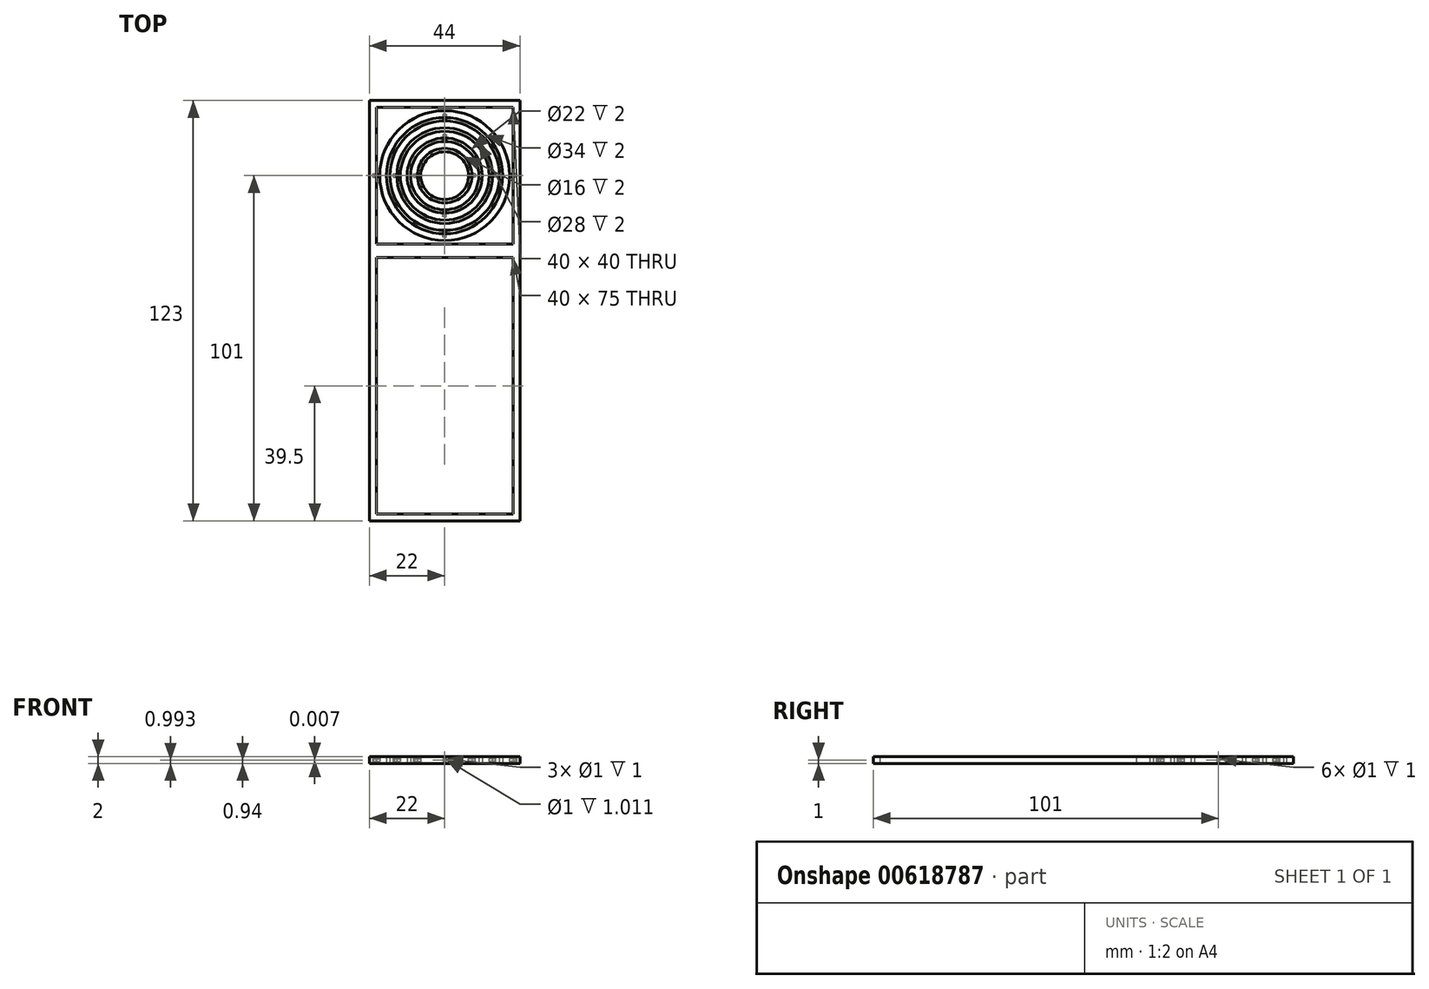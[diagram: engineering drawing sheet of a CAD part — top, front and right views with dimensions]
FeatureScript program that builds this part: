
annotation { "Feature Type Name" : "Feature", "Feature Type Description" : "" }
export const myFeature = defineFeature(function(context is Context, id is Id, definition is map)
    precondition{}
    {
        {
            var Q0;
            Q0=qCreatedBy(makeId("Top.planeOp"),FACE);
            var sketch = newSketch(context, id + "F0", { "sketchPlane" : qUnion([Q0])});
            skLineSegment(sketch, "E0.bottom", {"start": v(0, 0) * mm, "end": v(40, 0) * mm});
            skLineSegment(sketch, "E0.top", {"start": v(0, -75) * mm, "end": v(40, -75) * mm});
            skLineSegment(sketch, "E0.left", {"start": v(0, 0) * mm, "end": v(0, -75) * mm});
            skLineSegment(sketch, "E0.right", {"start": v(40, 0) * mm, "end": v(40, -75) * mm});
            skLineSegment(sketch, "E1.0", {"start": v(-2, -77) * mm, "end": v(42, -77) * mm});
            skLineSegment(sketch, "E1.1", {"start": v(-2, 2) * mm, "end": v(-2, -77) * mm});
            skLineSegment(sketch, "E1.2", {"start": v(-2, 2) * mm, "end": v(42, 2) * mm});
            skLineSegment(sketch, "E1.3", {"start": v(42, 2) * mm, "end": v(42, -77) * mm});
            skLineSegment(sketch, "E2.bottom", {"start": v(12.5, 0) * mm, "end": v(27.5, 0) * mm});
            skLineSegment(sketch, "E2.top", {"start": v(12.5, -30) * mm, "end": v(27.5, -30) * mm});
            skLineSegment(sketch, "E2.left", {"start": v(12.5, 0) * mm, "end": v(12.5, -30) * mm});
            skLineSegment(sketch, "E2.right", {"start": v(27.5, 0) * mm, "end": v(27.5, -30) * mm});
            skLineSegment(sketch, "E3.top", {"start": v(-2, 46) * mm, "end": v(42, 46) * mm});
            skLineSegment(sketch, "E3.left", {"start": v(-2, 2) * mm, "end": v(-2, 46) * mm});
            skLineSegment(sketch, "E3.right", {"start": v(42, 2) * mm, "end": v(42, 46) * mm});
            skLineSegment(sketch, "E4.0", {"start": v(40, 4) * mm, "end": v(40, 44) * mm});
            skLineSegment(sketch, "E4.1", {"start": v(0, 4) * mm, "end": v(40, 4) * mm});
            skLineSegment(sketch, "E4.2", {"start": v(0, 4) * mm, "end": v(0, 44) * mm});
            skLineSegment(sketch, "E4.3", {"start": v(0, 44) * mm, "end": v(40, 44) * mm});
            skLineSegment(sketch, "E5", {"start": v(20, 44) * mm, "end": v(20, 4) * mm, "construction": true});
            skLineSegment(sketch, "E6", {"start": v(0, 24) * mm, "end": v(40, 24) * mm, "construction": true});
            skCircle(sketch, "E7", {"center": v(20, 24) * mm, "radius": 19 * mm});
            skCircle(sketch, "E8.0", {"center": v(20, 24) * mm, "radius": 17 * mm});
            skCircle(sketch, "E9", {"center": v(20, 24) * mm, "radius": 16 * mm});
            skCircle(sketch, "E10.0", {"center": v(20, 24) * mm, "radius": 14 * mm});
            skCircle(sketch, "E11", {"center": v(20, 24) * mm, "radius": 13 * mm});
            skCircle(sketch, "E12.0", {"center": v(20, 24) * mm, "radius": 11 * mm});
            skCircle(sketch, "E13", {"center": v(20, 24) * mm, "radius": 10 * mm});
            skCircle(sketch, "E14.0", {"center": v(20, 24) * mm, "radius": 8 * mm});
            skCircle(sketch, "E15", {"center": v(20, 24) * mm, "radius": 7 * mm});
            skSolve(sketch);
        }
        {
            var Q0;
            Q0=makeQuery(id+"F0.imprint","IMPRINT",FACE,{"disambiguationData":[TD([[makeQuery(id+"F0.imprint","IMPRINT",EDGE,{"derivedFrom":sQuery(id+"F0.wireOp",EDGE,"E0.top")}),-1.0]])]});
            var Q1;
            Q1=makeQuery(id+"F0.imprint","IMPRINT",FACE,{"disambiguationData":[TD([[makeQuery(id+"F0.imprint","IMPRINT",EDGE,{"derivedFrom":sQuery(id+"F0.wireOp",EDGE,"E2.bottom")}),-1.0]])]});
            var Q2;
            Q2=makeQuery(id+"F0.imprint","IMPRINT",FACE,{"disambiguationData":[TD([[makeQuery(id+"F0.imprint","IMPRINT",EDGE,{"derivedFrom":sQuery(id+"F0.wireOp",EDGE,"E1.2")}),1.0]])]});
            var Q3;
            Q3=makeQuery(id+"F0.imprint","IMPRINT",FACE,{"disambiguationData":[TD([[makeQuery(id+"F0.imprint","IMPRINT",EDGE,{"derivedFrom":sQuery(id+"F0.wireOp",EDGE,"E7")}),1.0]])]});
            var Q4;
            Q4=makeQuery(id+"F0.imprint","IMPRINT",FACE,{"disambiguationData":[TD([[makeQuery(id+"F0.imprint","IMPRINT",EDGE,{"derivedFrom":sQuery(id+"F0.wireOp",EDGE,"E9")}),1.0]])]});
            var Q5;
            Q5=makeQuery(id+"F0.imprint","IMPRINT",FACE,{"disambiguationData":[TD([[makeQuery(id+"F0.imprint","IMPRINT",EDGE,{"derivedFrom":sQuery(id+"F0.wireOp",EDGE,"E11")}),1.0]])]});
            var Q6;
            Q6=makeQuery(id+"F0.imprint","IMPRINT",FACE,{"disambiguationData":[TD([[makeQuery(id+"F0.imprint","IMPRINT",EDGE,{"derivedFrom":sQuery(id+"F0.wireOp",EDGE,"E13")}),1.0]])]});
            var Q7;
            Q7=makeQuery(id+"F0.imprint","IMPRINT",FACE,{"disambiguationData":[TD([[makeQuery(id+"F0.imprint","IMPRINT",EDGE,{"derivedFrom":sQuery(id+"F0.wireOp",EDGE,"E15")}),1.0]])]});
            extrude(context, id + "F1", {"entities" : qUnion([Q0, Q1, Q2, Q3, Q4, Q5, Q6, Q7]), "depth" : 2 * mm, "offsetDistance" : 25 * mm});
        }
        {
            var Q0;
            Q0=qCreatedBy(makeId("Front.planeOp"),FACE);
            cPlane(context, id + "F2", {"entities" : qUnion([Q0]), "cplaneType" : CPlaneType.OFFSET, "offset" : 13 * mm, "oppositeDirection" : true, "width" : 150 * mm, "height" : 150 * mm});
        }
        {
            var Q0;
            Q0=qCreatedBy(id+"F2.planeOp",FACE);
            var sketch = newSketch(context, id + "F3", { "sketchPlane" : qUnion([Q0])});
            skLineSegment(sketch, "E16.0", {"start": v(9, 2) * mm, "end": v(31, 2) * mm});
            skLineSegment(sketch, "E17.0", {"start": v(9, 0) * mm, "end": v(31, 0) * mm});
            skLineSegment(sketch, "E18", {"start": v(20, 2) * mm, "end": v(20, 0) * mm, "construction": true});
            skLineSegment(sketch, "E19", {"start": v(19.5, 1) * mm, "end": v(20.6, 1) * mm, "construction": true});
            skCircle(sketch, "E20", {"center": v(20, 1) * mm, "radius": 0.5 * mm});
            skSolve(sketch);
        }
        {
            var Q0;
            Q0 = qSketchRegion(id + "F3", true);
            extrude(context, id + "F4", {"entities" : qUnion([Q0]), "operationType" : NewBodyOperationType.REMOVE, "depth" : 1 * mm, "offsetDistance" : 25 * mm, "hasSecondDirection" : true, "secondDirectionOppositeDirection" : true, "secondDirectionDepth" : .2 * mm});
        }
        {
            var Q0;
            Q0=qCreatedBy(makeId("Front.planeOp"),FACE);
            cPlane(context, id + "F5", {"entities" : qUnion([Q0]), "cplaneType" : CPlaneType.OFFSET, "offset" : 35 * mm, "oppositeDirection" : true, "width" : 150 * mm, "height" : 150 * mm});
        }
        {
            var Q0;
            Q0=qCreatedBy(id+"F5.planeOp",FACE);
            var sketch = newSketch(context, id + "F6", { "sketchPlane" : qUnion([Q0])});
            skLineSegment(sketch, "E21.0", {"start": v(9, 2) * mm, "end": v(31, 2) * mm});
            skLineSegment(sketch, "E22.0", {"start": v(9, 0) * mm, "end": v(31, 0) * mm});
            skLineSegment(sketch, "E23", {"start": v(20, 2) * mm, "end": v(20, 0) * mm, "construction": true});
            skLineSegment(sketch, "E24", {"start": v(20, 0) * mm, "end": v(20, -0.04) * mm, "construction": true});
            skLineSegment(sketch, "E25", {"start": v(20, 0.94) * mm, "end": v(19.44, 0.94) * mm, "construction": true});
            skLineSegment(sketch, "E26", {"start": v(19.44, 0.94) * mm, "end": v(20.62, 0.94) * mm, "construction": true});
            skCircle(sketch, "E27", {"center": v(20, 0.94) * mm, "radius": 0.5 * mm});
            skSolve(sketch);
        }
        {
            var Q0;
            Q0 = qSketchRegion(id + "F6", true);
            extrude(context, id + "F7", {"entities" : qUnion([Q0]), "operationType" : NewBodyOperationType.REMOVE, "oppositeDirection" : true, "depth" : 1 * mm, "offsetDistance" : 25 * mm, "hasSecondDirection" : true, "secondDirectionOppositeDirection" : false, "secondDirectionDepth" : .2 * mm});
        }
        {
            var Q0;
            Q0=qCreatedBy(makeId("Front.planeOp"),FACE);
            cPlane(context, id + "F8", {"entities" : qUnion([Q0]), "cplaneType" : CPlaneType.OFFSET, "offset" : 7 * mm, "oppositeDirection" : true, "width" : 150 * mm, "height" : 150 * mm});
        }
        {
            var Q0;
            Q0=qCreatedBy(id+"F8.planeOp",FACE);
            var sketch = newSketch(context, id + "F9", { "sketchPlane" : qUnion([Q0])});
            skLineSegment(sketch, "E28.0", {"start": v(3, 2) * mm, "end": v(37, 2) * mm});
            skLineSegment(sketch, "E29.0", {"start": v(3, 0) * mm, "end": v(37, 0) * mm});
            skLineSegment(sketch, "E30", {"start": v(20, 0) * mm, "end": v(20, 2) * mm, "construction": true});
            skLineSegment(sketch, "E31", {"start": v(20, 1) * mm, "end": v(19.29, 1) * mm, "construction": true});
            skCircle(sketch, "E32", {"center": v(20, 1) * mm, "radius": 0.5 * mm});
            skSolve(sketch);
        }
        {
            var Q0;
            Q0 = qSketchRegion(id + "F9", true);
            extrude(context, id + "F10", {"entities" : qUnion([Q0]), "operationType" : NewBodyOperationType.REMOVE, "depth" : 1 * mm, "offsetDistance" : 25 * mm, "hasSecondDirection" : true, "secondDirectionOppositeDirection" : true, "secondDirectionDepth" : .2 * mm});
        }
        {
            var Q0;
            Q0=qCreatedBy(makeId("Front.planeOp"),FACE);
            cPlane(context, id + "F11", {"entities" : qUnion([Q0]), "cplaneType" : CPlaneType.OFFSET, "offset" : 41 * mm, "oppositeDirection" : true, "width" : 150 * mm, "height" : 150 * mm});
        }
        {
            var Q0;
            Q0=qCreatedBy(id+"F11.planeOp",FACE);
            var sketch = newSketch(context, id + "F12", { "sketchPlane" : qUnion([Q0])});
            skLineSegment(sketch, "E33.0", {"start": v(3, 2) * mm, "end": v(37, 2) * mm});
            skLineSegment(sketch, "E34.0", {"start": v(3, 0) * mm, "end": v(37, 0) * mm});
            skLineSegment(sketch, "E35", {"start": v(20, 0) * mm, "end": v(20, 2) * mm, "construction": true});
            skLineSegment(sketch, "E36", {"start": v(19.44, 1) * mm, "end": v(20, 1) * mm, "construction": true});
            skCircle(sketch, "E37", {"center": v(20, 1) * mm, "radius": 0.5 * mm});
            skSolve(sketch);
        }
        {
            var Q0;
            Q0 = qSketchRegion(id + "F12", true);
            extrude(context, id + "F13", {"entities" : qUnion([Q0]), "operationType" : NewBodyOperationType.REMOVE, "oppositeDirection" : true, "depth" : 1 * mm, "offsetDistance" : 25 * mm, "hasSecondDirection" : true, "secondDirectionOppositeDirection" : false, "secondDirectionDepth" : .2 * mm});
        }
        {
            var Q0;
            Q0=qCreatedBy(makeId("Right.planeOp"),FACE);
            cPlane(context, id + "F14", {"entities" : qUnion([Q0]), "cplaneType" : CPlaneType.OFFSET, "offset" : 6 * mm, "width" : 150 * mm, "height" : 150 * mm});
        }
        {
            var Q0;
            Q0=qCreatedBy(id+"F14.planeOp",FACE);
            var sketch = newSketch(context, id + "F15", { "sketchPlane" : qUnion([Q0])});
            skLineSegment(sketch, "E38.0", {"start": v(10, 2) * mm, "end": v(38, 2) * mm});
            skLineSegment(sketch, "E39.0", {"start": v(10, 0) * mm, "end": v(38, 0) * mm});
            skLineSegment(sketch, "E40", {"start": v(24.24, 1) * mm, "end": v(23.72, 1) * mm, "construction": true});
            skCircle(sketch, "E41", {"center": v(24, 1) * mm, "radius": 0.5 * mm});
            skSolve(sketch);
        }
        {
            var Q0;
            Q0=makeQuery(id+"F15.imprint","IMPRINT",FACE,{"disambiguationData":[TD([[makeQuery(id+"F15.imprint","IMPRINT",EDGE,{"derivedFrom":sQuery(id+"F15.wireOp",EDGE,"E41")}),1.0]])]});
            extrude(context, id + "F16", {"entities" : qUnion([Q0]), "operationType" : NewBodyOperationType.REMOVE, "oppositeDirection" : true, "depth" : 1 * mm, "offsetDistance" : 25 * mm, "hasSecondDirection" : true, "secondDirectionOppositeDirection" : false, "secondDirectionDepth" : .2 * mm});
        }
        {
            var Q0;
            Q0=qCreatedBy(makeId("Right.planeOp"),FACE);
            cPlane(context, id + "F17", {"entities" : qUnion([Q0]), "cplaneType" : CPlaneType.OFFSET, "offset" : 34 * mm, "width" : 150 * mm, "height" : 150 * mm});
        }
        {
            var Q0;
            Q0=qCreatedBy(id+"F17.planeOp",FACE);
            var sketch = newSketch(context, id + "F18", { "sketchPlane" : qUnion([Q0])});
            skLineSegment(sketch, "E42.0", {"start": v(10, 0) * mm, "end": v(38, 0) * mm});
            skLineSegment(sketch, "E43.0", {"start": v(10, 2) * mm, "end": v(38, 2) * mm});
            skLineSegment(sketch, "E44", {"start": v(24, 0) * mm, "end": v(24, 2) * mm, "construction": true});
            skLineSegment(sketch, "E45", {"start": v(24.2, 1) * mm, "end": v(23.66, 1) * mm, "construction": true});
            skCircle(sketch, "E46", {"center": v(24, 1) * mm, "radius": 0.5 * mm});
            skSolve(sketch);
        }
        {
            var Q0;
            Q0 = qSketchRegion(id + "F18", true);
            extrude(context, id + "F19", {"entities" : qUnion([Q0]), "operationType" : NewBodyOperationType.REMOVE, "depth" : 1 * mm, "offsetDistance" : 25 * mm, "hasSecondDirection" : true, "secondDirectionOppositeDirection" : true, "secondDirectionDepth" : .2 * mm});
        }
        {
            var Q0;
            Q0=makeQuery(id+"F1.opExtrude","SWEPT_FACE",FACE,{"disambiguationData":[OSD([sQuery(id+"F0.wireOp",EDGE,"E4.2")])]});
            var sketch = newSketch(context, id + "F20", { "sketchPlane" : qUnion([Q0])});
            skPoint(sketch, "E47.0", {"position": v(24, 0) * mm});
            skLineSegment(sketch, "E48", {"start": v(24, 0) * mm, "end": v(24, 2) * mm, "construction": true});
            skLineSegment(sketch, "E49", {"start": v(24.56, 1) * mm, "end": v(23.4, 1) * mm, "construction": true});
            skCircle(sketch, "E50", {"center": v(24, 1) * mm, "radius": 0.5 * mm});
            skSolve(sketch);
        }
        {
            var Q0;
            Q0=makeQuery(id+"F20.imprint","IMPRINT",FACE,{"disambiguationData":[TD([[makeQuery(id+"F20.imprint","IMPRINT",EDGE,{"derivedFrom":sQuery(id+"F20.wireOp",EDGE,"E50")}),1.0]])]});
            extrude(context, id + "F21", {"entities" : qUnion([Q0]), "operationType" : NewBodyOperationType.REMOVE, "oppositeDirection" : true, "depth" : 1 * mm, "offsetDistance" : 25 * mm});
        }
        {
            var Q0;
            Q0=makeQuery(id+"F1.opExtrude","SWEPT_FACE",FACE,{"disambiguationData":[OSD([sQuery(id+"F0.wireOp",EDGE,"E4.0")])]});
            var sketch = newSketch(context, id + "F22", { "sketchPlane" : qUnion([Q0])});
            skLineSegment(sketch, "E51", {"start": v(-24, 0) * mm, "end": v(-24, 2) * mm, "construction": true});
            skLineSegment(sketch, "E52", {"start": v(-24.46, 1) * mm, "end": v(-23.58, 1) * mm, "construction": true});
            skCircle(sketch, "E53", {"center": v(-24, 1) * mm, "radius": 0.5 * mm});
            skSolve(sketch);
        }
        {
            var Q0;
            Q0=makeQuery(id+"F22.imprint","IMPRINT",FACE,{"disambiguationData":[TD([[makeQuery(id+"F22.imprint","IMPRINT",EDGE,{"derivedFrom":sQuery(id+"F22.wireOp",EDGE,"E53")}),1.0]])]});
            extrude(context, id + "F23", {"entities" : qUnion([Q0]), "operationType" : NewBodyOperationType.REMOVE, "oppositeDirection" : true, "depth" : 1 * mm, "offsetDistance" : 25 * mm});
        }
        {
            var Q0;
            Q0=qCreatedBy(makeId("Right.planeOp"),FACE);
            cPlane(context, id + "F24", {"entities" : qUnion([Q0]), "cplaneType" : CPlaneType.OFFSET, "offset" : 1 * mm, "width" : 150 * mm, "height" : 150 * mm});
        }
        {
            var Q0;
            Q0=qCreatedBy(id+"F24.planeOp",FACE);
            var sketch = newSketch(context, id + "F25", { "sketchPlane" : qUnion([Q0])});
            skPoint(sketch, "E54.0", {"position": v(24, 0) * mm});
            skLineSegment(sketch, "E55", {"start": v(24, 0) * mm, "end": v(24, 2) * mm, "construction": true});
            skLineSegment(sketch, "E56", {"start": v(24.48, 1) * mm, "end": v(23.55, 1) * mm, "construction": true});
            skCircle(sketch, "E57", {"center": v(24, 1) * mm, "radius": 0.35 * mm});
            skSolve(sketch);
        }
        {
            var Q0;
            Q0=qCreatedBy(makeId("Right.planeOp"),FACE);
            cPlane(context, id + "F26", {"entities" : qUnion([Q0]), "cplaneType" : CPlaneType.OFFSET, "offset" : 12 * mm, "width" : 150 * mm, "height" : 150 * mm});
        }
        {
            var Q0;
            Q0=qCreatedBy(id+"F26.planeOp",FACE);
            var sketch = newSketch(context, id + "F27", { "sketchPlane" : qUnion([Q0])});
            skLineSegment(sketch, "E58.0", {"start": v(16, 2) * mm, "end": v(32, 2) * mm});
            skLineSegment(sketch, "E59.0", {"start": v(16, 0) * mm, "end": v(32, 0) * mm});
            skLineSegment(sketch, "E60", {"start": v(24, 2) * mm, "end": v(24, 0) * mm, "construction": true});
            skLineSegment(sketch, "E61", {"start": v(24, 0) * mm, "end": v(23.98, -0.05) * mm, "construction": true});
            skCircle(sketch, "E62", {"center": v(24, 1) * mm, "radius": 0.5 * mm});
            skSolve(sketch);
        }
        {
            var Q0;
            Q0 = qSketchRegion(id + "F27", true);
            extrude(context, id + "F28", {"entities" : qUnion([Q0]), "operationType" : NewBodyOperationType.REMOVE, "oppositeDirection" : true, "depth" : 1 * mm, "offsetDistance" : 25 * mm, "hasSecondDirection" : true, "secondDirectionOppositeDirection" : false, "secondDirectionDepth" : .2 * mm});
        }
        {
            var Q0;
            Q0=qCreatedBy(makeId("Right.planeOp"),FACE);
            cPlane(context, id + "F29", {"entities" : qUnion([Q0]), "cplaneType" : CPlaneType.OFFSET, "offset" : 28 * mm, "width" : 150 * mm, "height" : 150 * mm});
        }
        {
            var Q0;
            Q0=qCreatedBy(id+"F29.planeOp",FACE);
            var sketch = newSketch(context, id + "F30", { "sketchPlane" : qUnion([Q0])});
            skLineSegment(sketch, "E63.0", {"start": v(16, 2) * mm, "end": v(32, 2) * mm});
            skLineSegment(sketch, "E64.0", {"start": v(16, 0) * mm, "end": v(32, 0) * mm});
            skLineSegment(sketch, "E65", {"start": v(24, 2) * mm, "end": v(24, 0) * mm, "construction": true});
            skLineSegment(sketch, "E66", {"start": v(24, 0) * mm, "end": v(24.02, -0.07) * mm, "construction": true});
            skCircle(sketch, "E67", {"center": v(24, 1) * mm, "radius": 0.5 * mm});
            skSolve(sketch);
        }
        {
            var Q0;
            Q0 = qSketchRegion(id + "F30", true);
            extrude(context, id + "F31", {"entities" : qUnion([Q0]), "operationType" : NewBodyOperationType.REMOVE, "depth" : 1 * mm, "offsetDistance" : 25 * mm, "hasSecondDirection" : true, "secondDirectionOppositeDirection" : true, "secondDirectionDepth" : .2 * mm});
        }
        {
            var Q0;
            Q0=makeQuery(id+"F25.imprint","IMPRINT",FACE,{"disambiguationData":[TD([[makeQuery(id+"F25.imprint","IMPRINT",EDGE,{"derivedFrom":sQuery(id+"F25.wireOp",EDGE,"E57")}),1.0]])]});
            extrude(context, id + "F32", {"entities" : qUnion([Q0]), "operationType" : NewBodyOperationType.ADD, "oppositeDirection" : true, "depth" : 1.7 * mm, "offsetDistance" : 25 * mm, "hasSecondDirection" : true, "secondDirectionOppositeDirection" : false, "secondDirectionDepth" : .2 * mm});
        }
        {
            var Q0;
            Q0=qCreatedBy(makeId("Right.planeOp"),FACE);
            cPlane(context, id + "F33", {"entities" : qUnion([Q0]), "cplaneType" : CPlaneType.OFFSET, "offset" : 39 * mm, "width" : 150 * mm, "height" : 150 * mm});
        }
        {
            var Q0;
            Q0=qCreatedBy(id+"F33.planeOp",FACE);
            var sketch = newSketch(context, id + "F34", { "sketchPlane" : qUnion([Q0])});
            skLineSegment(sketch, "E68.0", {"start": v(5, 0) * mm, "end": v(43, 0) * mm});
            skLineSegment(sketch, "E69.0", {"start": v(5, 2) * mm, "end": v(43, 2) * mm});
            skPoint(sketch, "E70.0", {"position": v(24, 0) * mm});
            skLineSegment(sketch, "E71", {"start": v(24, 0) * mm, "end": v(24, 2) * mm, "construction": true});
            skLineSegment(sketch, "E72", {"start": v(24.56, 1) * mm, "end": v(23.48, 1) * mm, "construction": true});
            skCircle(sketch, "E73", {"center": v(24, 1) * mm, "radius": 0.35 * mm});
            skSolve(sketch);
        }
        {
            var Q0;
            Q0=makeQuery(id+"F34.imprint","IMPRINT",FACE,{"disambiguationData":[TD([[makeQuery(id+"F34.imprint","IMPRINT",EDGE,{"derivedFrom":sQuery(id+"F34.wireOp",EDGE,"E73")}),1.0]])]});
            extrude(context, id + "F35", {"entities" : qUnion([Q0]), "operationType" : NewBodyOperationType.ADD, "depth" : 1.7 * mm, "offsetDistance" : 25 * mm, "hasSecondDirection" : true, "secondDirectionOppositeDirection" : true, "secondDirectionDepth" : .2 * mm});
        }
        {
            var Q0;
            Q0=qCreatedBy(makeId("Right.planeOp"),FACE);
            cPlane(context, id + "F36", {"entities" : qUnion([Q0]), "cplaneType" : CPlaneType.OFFSET, "offset" : 7 * mm, "width" : 150 * mm, "height" : 150 * mm});
        }
        {
            var Q0;
            Q0=qCreatedBy(id+"F36.planeOp",FACE);
            var sketch = newSketch(context, id + "F37", { "sketchPlane" : qUnion([Q0])});
            skLineSegment(sketch, "E74.0", {"start": v(5, 0) * mm, "end": v(43, 0) * mm});
            skPoint(sketch, "E75.0", {"position": v(24, 0) * mm});
            skLineSegment(sketch, "E76.0", {"start": v(11, 2) * mm, "end": v(37, 2) * mm});
            skLineSegment(sketch, "E77", {"start": v(24, 0) * mm, "end": v(24, 2) * mm, "construction": true});
            skLineSegment(sketch, "E78", {"start": v(24.67, 1) * mm, "end": v(23.38, 1) * mm, "construction": true});
            skCircle(sketch, "E79", {"center": v(24, 1) * mm, "radius": 0.35 * mm});
            skSolve(sketch);
        }
        {
            var Q0;
            Q0=makeQuery(id+"F37.imprint","IMPRINT",FACE,{"disambiguationData":[TD([[makeQuery(id+"F37.imprint","IMPRINT",EDGE,{"derivedFrom":sQuery(id+"F37.wireOp",EDGE,"E79")}),1.0]])]});
            extrude(context, id + "F38", {"entities" : qUnion([Q0]), "operationType" : NewBodyOperationType.ADD, "oppositeDirection" : true, "depth" : 1.7 * mm, "offsetDistance" : 25 * mm, "hasSecondDirection" : true, "secondDirectionOppositeDirection" : false, "secondDirectionDepth" : .2 * mm});
        }
        {
            var Q0;
            Q0=qCreatedBy(makeId("Right.planeOp"),FACE);
            cPlane(context, id + "F39", {"entities" : qUnion([Q0]), "cplaneType" : CPlaneType.OFFSET, "offset" : 33 * mm, "width" : 150 * mm, "height" : 150 * mm});
        }
        {
            var Q0;
            Q0=qCreatedBy(id+"F39.planeOp",FACE);
            var sketch = newSketch(context, id + "F40", { "sketchPlane" : qUnion([Q0])});
            skLineSegment(sketch, "E80.0", {"start": v(11, 2) * mm, "end": v(37, 2) * mm});
            skLineSegment(sketch, "E81.0", {"start": v(5, 0) * mm, "end": v(43, 0) * mm});
            skPoint(sketch, "E82.0", {"position": v(24, 0) * mm});
            skLineSegment(sketch, "E83", {"start": v(24, 0) * mm, "end": v(24, 2) * mm, "construction": true});
            skLineSegment(sketch, "E84", {"start": v(22.86, 1) * mm, "end": v(25.17, 1) * mm, "construction": true});
            skCircle(sketch, "E85", {"center": v(24, 1) * mm, "radius": 0.35 * mm});
            skSolve(sketch);
        }
        {
            var Q0;
            Q0=makeQuery(id+"F40.imprint","IMPRINT",FACE,{"disambiguationData":[TD([[makeQuery(id+"F40.imprint","IMPRINT",EDGE,{"derivedFrom":sQuery(id+"F40.wireOp",EDGE,"E85")}),1.0]])]});
            extrude(context, id + "F41", {"entities" : qUnion([Q0]), "operationType" : NewBodyOperationType.ADD, "depth" : 1.7 * mm, "offsetDistance" : 25 * mm, "hasSecondDirection" : true, "secondDirectionOppositeDirection" : true, "secondDirectionDepth" : .2 * mm});
        }
        {
            var Q0;
            Q0=qCreatedBy(makeId("Right.planeOp"),FACE);
            cPlane(context, id + "F42", {"entities" : qUnion([Q0]), "cplaneType" : CPlaneType.OFFSET, "offset" : 13 * mm, "width" : 150 * mm, "height" : 150 * mm});
        }
        {
            var Q0;
            Q0=qCreatedBy(id+"F42.planeOp",FACE);
            var sketch = newSketch(context, id + "F43", { "sketchPlane" : qUnion([Q0])});
            skLineSegment(sketch, "E86.0", {"start": v(17, 2) * mm, "end": v(31, 2) * mm});
            skLineSegment(sketch, "E87.0", {"start": v(5, 0) * mm, "end": v(43, 0) * mm});
            skPoint(sketch, "E88.0", {"position": v(24, 0) * mm});
            skLineSegment(sketch, "E89", {"start": v(24, 0) * mm, "end": v(24, 2) * mm, "construction": true});
            skLineSegment(sketch, "E90", {"start": v(24.58, 1) * mm, "end": v(23.34, 1) * mm, "construction": true});
            skCircle(sketch, "E91", {"center": v(24, 1) * mm, "radius": 0.35 * mm});
            skSolve(sketch);
        }
        {
            var Q0;
            Q0=makeQuery(id+"F43.imprint","IMPRINT",FACE,{"disambiguationData":[TD([[makeQuery(id+"F43.imprint","IMPRINT",EDGE,{"derivedFrom":sQuery(id+"F43.wireOp",EDGE,"E91")}),1.0]])]});
            extrude(context, id + "F44", {"entities" : qUnion([Q0]), "operationType" : NewBodyOperationType.ADD, "oppositeDirection" : true, "depth" : 1.7 * mm, "offsetDistance" : 25 * mm, "hasSecondDirection" : true, "secondDirectionOppositeDirection" : false, "secondDirectionDepth" : .2 * mm});
        }
        {
            var Q0;
            Q0=qCreatedBy(makeId("Right.planeOp"),FACE);
            cPlane(context, id + "F45", {"entities" : qUnion([Q0]), "cplaneType" : CPlaneType.OFFSET, "offset" : 27 * mm, "width" : 150 * mm, "height" : 150 * mm});
        }
        {
            var Q0;
            Q0=qCreatedBy(id+"F45.planeOp",FACE);
            var sketch = newSketch(context, id + "F46", { "sketchPlane" : qUnion([Q0])});
            skLineSegment(sketch, "E92.0", {"start": v(17, 2) * mm, "end": v(31, 2) * mm});
            skLineSegment(sketch, "E93.0", {"start": v(5, 0) * mm, "end": v(43, 0) * mm});
            skPoint(sketch, "E94.0", {"position": v(24, 0) * mm});
            skLineSegment(sketch, "E95", {"start": v(24, 0) * mm, "end": v(24, 2) * mm, "construction": true});
            skLineSegment(sketch, "E96", {"start": v(23.22, 1) * mm, "end": v(24.71, 1) * mm, "construction": true});
            skCircle(sketch, "E97", {"center": v(24, 1) * mm, "radius": 0.35 * mm});
            skSolve(sketch);
        }
        {
            var Q0;
            Q0=makeQuery(id+"F46.imprint","IMPRINT",FACE,{"disambiguationData":[TD([[makeQuery(id+"F46.imprint","IMPRINT",EDGE,{"derivedFrom":sQuery(id+"F46.wireOp",EDGE,"E97")}),1.0]])]});
            extrude(context, id + "F47", {"entities" : qUnion([Q0]), "operationType" : NewBodyOperationType.ADD, "depth" : 1.7 * mm, "offsetDistance" : 25 * mm, "hasSecondDirection" : true, "secondDirectionOppositeDirection" : true, "secondDirectionDepth" : .2 * mm});
        }
        {
            var Q0;
            Q0=qCreatedBy(makeId("Front.planeOp"),FACE);
            cPlane(context, id + "F48", {"entities" : qUnion([Q0]), "cplaneType" : CPlaneType.OFFSET, "offset" : 8 * mm, "oppositeDirection" : true, "width" : 150 * mm, "height" : 150 * mm});
        }
        {
            var Q0;
            Q0=qCreatedBy(id+"F48.planeOp",FACE);
            var sketch = newSketch(context, id + "F49", { "sketchPlane" : qUnion([Q0])});
            skPoint(sketch, "E98.0", {"position": v(20, 0) * mm});
            skLineSegment(sketch, "E99.0", {"start": v(1, 2) * mm, "end": v(39, 2) * mm});
            skLineSegment(sketch, "E100.0", {"start": v(4, 0) * mm, "end": v(36, 0) * mm});
            skLineSegment(sketch, "E101", {"start": v(20, 0) * mm, "end": v(20, 2) * mm, "construction": true});
            skLineSegment(sketch, "E102", {"start": v(19.28, 1) * mm, "end": v(20.84, 1) * mm, "construction": true});
            skCircle(sketch, "E103", {"center": v(20, 1) * mm, "radius": 0.35 * mm});
            skSolve(sketch);
        }
        {
            var Q0;
            Q0 = qSketchRegion(id + "F49", true);
            extrude(context, id + "F50", {"entities" : qUnion([Q0]), "operationType" : NewBodyOperationType.ADD, "depth" : 1.7 * mm, "offsetDistance" : 25 * mm, "hasSecondDirection" : true, "secondDirectionOppositeDirection" : true, "secondDirectionDepth" : .2 * mm});
        }
        {
            var Q0;
            Q0=qCreatedBy(makeId("Front.planeOp"),FACE);
            cPlane(context, id + "F51", {"entities" : qUnion([Q0]), "cplaneType" : CPlaneType.OFFSET, "offset" : 40 * mm, "oppositeDirection" : true, "width" : 150 * mm, "height" : 150 * mm});
        }
        {
            var Q0;
            Q0=qCreatedBy(id+"F51.planeOp",FACE);
            var sketch = newSketch(context, id + "F52", { "sketchPlane" : qUnion([Q0])});
            skLineSegment(sketch, "E104.0", {"start": v(4, 2) * mm, "end": v(36, 2) * mm});
            skLineSegment(sketch, "E105.0", {"start": v(4, 0) * mm, "end": v(36, 0) * mm});
            skPoint(sketch, "E106.0", {"position": v(20, 0) * mm});
            skLineSegment(sketch, "E107", {"start": v(20, 0) * mm, "end": v(20, 2) * mm, "construction": true});
            skLineSegment(sketch, "E108", {"start": v(20.72, 1) * mm, "end": v(19.2, 1) * mm, "construction": true});
            skCircle(sketch, "E109", {"center": v(20, 1) * mm, "radius": 0.35 * mm});
            skSolve(sketch);
        }
        {
            var Q0;
            Q0=makeQuery(id+"F52.imprint","IMPRINT",FACE,{"disambiguationData":[TD([[makeQuery(id+"F52.imprint","IMPRINT",EDGE,{"derivedFrom":sQuery(id+"F52.wireOp",EDGE,"E109")}),1.0]])]});
            extrude(context, id + "F53", {"entities" : qUnion([Q0]), "operationType" : NewBodyOperationType.ADD, "oppositeDirection" : true, "depth" : 1.7 * mm, "offsetDistance" : 25 * mm, "hasSecondDirection" : true, "secondDirectionOppositeDirection" : false, "secondDirectionDepth" : .2 * mm});
        }
        {
            var Q0;
            Q0=qCreatedBy(makeId("Front.planeOp"),FACE);
            cPlane(context, id + "F54", {"entities" : qUnion([Q0]), "cplaneType" : CPlaneType.OFFSET, "offset" : 14 * mm, "oppositeDirection" : true, "width" : 150 * mm, "height" : 150 * mm});
        }
        {
            var Q0;
            Q0=qCreatedBy(id+"F54.planeOp",FACE);
            var sketch = newSketch(context, id + "F55", { "sketchPlane" : qUnion([Q0])});
            skLineSegment(sketch, "E110.0", {"start": v(10, 2) * mm, "end": v(30, 2) * mm});
            skLineSegment(sketch, "E111.0", {"start": v(6, 0) * mm, "end": v(34, 0) * mm});
            skPoint(sketch, "E111.1", {"position": v(20, 0) * mm});
            skLineSegment(sketch, "E112", {"start": v(20, 0) * mm, "end": v(20, 2) * mm, "construction": true});
            skLineSegment(sketch, "E113", {"start": v(19.5, 1) * mm, "end": v(20.45, 1) * mm, "construction": true});
            skCircle(sketch, "E114", {"center": v(20, 1) * mm, "radius": 0.35 * mm});
            skSolve(sketch);
        }
        {
            var Q0;
            Q0=makeQuery(id+"F55.imprint","IMPRINT",FACE,{"disambiguationData":[TD([[makeQuery(id+"F55.imprint","IMPRINT",EDGE,{"derivedFrom":sQuery(id+"F55.wireOp",EDGE,"E114")}),1.0]])]});
            extrude(context, id + "F56", {"entities" : qUnion([Q0]), "operationType" : NewBodyOperationType.ADD, "depth" : 1.7 * mm, "offsetDistance" : 25 * mm, "hasSecondDirection" : true, "secondDirectionOppositeDirection" : true, "secondDirectionDepth" : .2 * mm});
        }
        {
            var Q0;
            Q0=qCreatedBy(makeId("Front.planeOp"),FACE);
            cPlane(context, id + "F57", {"entities" : qUnion([Q0]), "cplaneType" : CPlaneType.OFFSET, "offset" : 34 * mm, "oppositeDirection" : true, "width" : 150 * mm, "height" : 150 * mm});
        }
        {
            var Q0;
            Q0=qCreatedBy(id+"F57.planeOp",FACE);
            var sketch = newSketch(context, id + "F58", { "sketchPlane" : qUnion([Q0])});
            skLineSegment(sketch, "E115.0", {"start": v(10, 2) * mm, "end": v(30, 2) * mm});
            skPoint(sketch, "E116.0", {"position": v(20, 0) * mm});
            skLineSegment(sketch, "E117", {"start": v(20, 0) * mm, "end": v(20, 2) * mm, "construction": true});
            skLineSegment(sketch, "E118", {"start": v(20.83, 1) * mm, "end": v(19.18, 1) * mm, "construction": true});
            skCircle(sketch, "E119", {"center": v(20, 1) * mm, "radius": 0.35 * mm});
            skSolve(sketch);
        }
        {
            var Q0;
            Q0=makeQuery(id+"F58.imprint","IMPRINT",FACE,{"disambiguationData":[TD([[makeQuery(id+"F58.imprint","IMPRINT",EDGE,{"derivedFrom":sQuery(id+"F58.wireOp",EDGE,"E119")}),1.0]])]});
            extrude(context, id + "F59", {"entities" : qUnion([Q0]), "operationType" : NewBodyOperationType.ADD, "oppositeDirection" : true, "depth" : 1.7 * mm, "offsetDistance" : 25 * mm, "hasSecondDirection" : true, "secondDirectionOppositeDirection" : false, "secondDirectionDepth" : .2 * mm});
        }
    });
